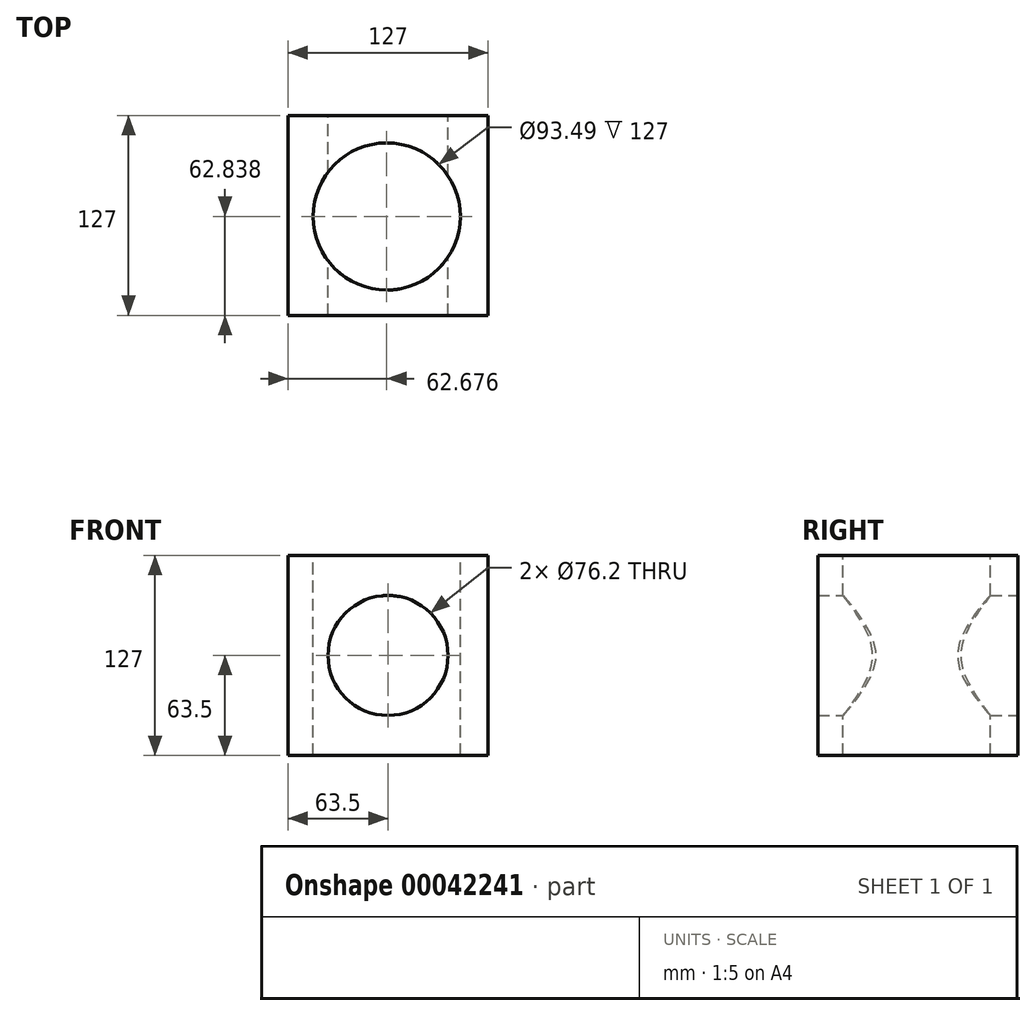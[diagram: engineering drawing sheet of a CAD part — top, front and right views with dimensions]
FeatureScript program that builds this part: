
annotation { "Feature Type Name" : "Feature", "Feature Type Description" : "" }
export const myFeature = defineFeature(function(context is Context, id is Id, definition is map)
    precondition{}
    {
        {
            var Q0;
            Q0=qCreatedBy(makeId("Top.planeOp"),FACE);
            var sketch = newSketch(context, id + "F0", { "sketchPlane" : qUnion([Q0])});
            skLineSegment(sketch, "E0", {"start": v(0, 127) * mm, "end": v(127, 127) * mm});
            skLineSegment(sketch, "E1", {"start": v(127, 127) * mm, "end": v(127, 0) * mm});
            skLineSegment(sketch, "E2", {"start": v(0, 127) * mm, "end": v(0, 0) * mm});
            skLineSegment(sketch, "E3", {"start": v(127, 0) * mm, "end": v(0, 0) * mm});
            skSolve(sketch);
        }
        {
            var Q0;
            Q0=makeQuery(id+"F0.imprint","IMPRINT",FACE,{"disambiguationData":[TD([[makeQuery(id+"F0.imprint","IMPRINT",EDGE,{"derivedFrom":sQuery(id+"F0.wireOp",EDGE,"E0")}),-1.0]])]});
            extrude(context, id + "F1", {"entities" : qUnion([Q0]), "depth" : 127 * mm});
        }
        {
            var Q0;
            Q0=makeQuery(id+"F1.opExtrude","CAP_FACE",FACE,{"disambiguationData":[OSD([sQuery(id+"F0.wireOp",EDGE,"E0"),sQuery(id+"F0.wireOp",EDGE,"E1"),sQuery(id+"F0.wireOp",EDGE,"E2"),sQuery(id+"F0.wireOp",EDGE,"E3")])],"isStart":false});
            var sketch = newSketch(context, id + "F2", { "sketchPlane" : qUnion([Q0])});
            skSolve(sketch);
        }
        {
            var Q0;
            Q0=makeQuery(id+"F2.imprint","IMPRINT",FACE,{"disambiguationData":[TD([[makeQuery(id+"F2.imprint","IMPRINT",EDGE,{"derivedFrom":makeQuery(id+"F1.opExtrude","CAP_EDGE",EDGE,{"disambiguationData":[OSD([sQuery(id+"F0.wireOp",EDGE,"E0")])],"isStart":false})}),-1.0]])]});
            var sketch = newSketch(context, id + "F3", { "sketchPlane" : qUnion([Q0])});
            skLineSegment(sketch, "E4", {"start": v(0, 125.84) * mm, "end": v(125.19, 0) * mm});
            skLineSegment(sketch, "E5", {"start": v(126.83, 127.16) * mm, "end": v(0, 0) * mm});
            skCircle(sketch, "E6", {"center": v(62.68, 62.84) * mm, "radius": 46.75 * mm});
            skSolve(sketch);
        }
        {
            var Q0;
            Q0 = qSketchRegion(id + "F3", true);
            extrude(context, id + "F4", {"entities" : qUnion([Q0]), "operationType" : NewBodyOperationType.REMOVE, "oppositeDirection" : true, "depth" : 127 * mm});
        }
        {
            var Q0;
            Q0=makeQuery(id+"F1.opExtrude","SWEPT_FACE",FACE,{"disambiguationData":[OSD([sQuery(id+"F0.wireOp",EDGE,"E1")])]});
            var sketch = newSketch(context, id + "F5", { "sketchPlane" : qUnion([Q0])});
            skLineSegment(sketch, "E7", {"start": v(0, 127) * mm, "end": v(127, 0) * mm});
            skLineSegment(sketch, "E8", {"start": v(0, 0) * mm, "end": v(127, 127) * mm});
            skCircle(sketch, "E9", {"center": v(63.5, 63.5) * mm, "radius": 37.62 * mm});
            skSolve(sketch);
        }
        {
            var Q0;
            Q0 = qSketchRegion(id + "F5", true);
            extrude(context, id + "F6", {"entities" : qUnion([Q0]), "operationType" : NewBodyOperationType.REMOVE, "depth" : 127 * mm});
        }
        {
            var Q0;
            Q0=makeQuery(id+"F1.opExtrude","SWEPT_FACE",FACE,{"disambiguationData":[OSD([sQuery(id+"F0.wireOp",EDGE,"E1")])]});
            var sketch = newSketch(context, id + "F7", { "sketchPlane" : qUnion([Q0])});
            skLineSegment(sketch, "E10", {"start": v(0, 127) * mm, "end": v(127, 0) * mm});
            skLineSegment(sketch, "E11", {"start": v(127, 127) * mm, "end": v(0, 0) * mm});
            skCircle(sketch, "E12", {"center": v(63.5, 63.5) * mm, "radius": 40.98 * mm});
            skSolve(sketch);
        }
        {
            var Q0;
            Q0 = qSketchRegion(id + "F7", true);
            extrude(context, id + "F8", {"entities" : qUnion([Q0]), "operationType" : NewBodyOperationType.REMOVE, "depth" : 127 * mm});
        }
        {
            var Q0;
            Q0=makeQuery(id+"F1.opExtrude","SWEPT_FACE",FACE,{"disambiguationData":[OSD([sQuery(id+"F0.wireOp",EDGE,"E0")])]});
            var sketch = newSketch(context, id + "F9", { "sketchPlane" : qUnion([Q0])});
            skLineSegment(sketch, "E13", {"start": v(-127, 0) * mm, "end": v(0, 127) * mm});
            skLineSegment(sketch, "E14", {"start": v(0, 0) * mm, "end": v(-127, 127) * mm});
            skCircle(sketch, "E15", {"center": v(-63.5, 63.5) * mm, "radius": 38.1 * mm});
            skSolve(sketch);
        }
        {
            var Q0;
            Q0 = qSketchRegion(id + "F9", true);
            extrude(context, id + "F10", {"entities" : qUnion([Q0]), "operationType" : NewBodyOperationType.REMOVE, "oppositeDirection" : true, "depth" : 127 * mm});
        }
    });
